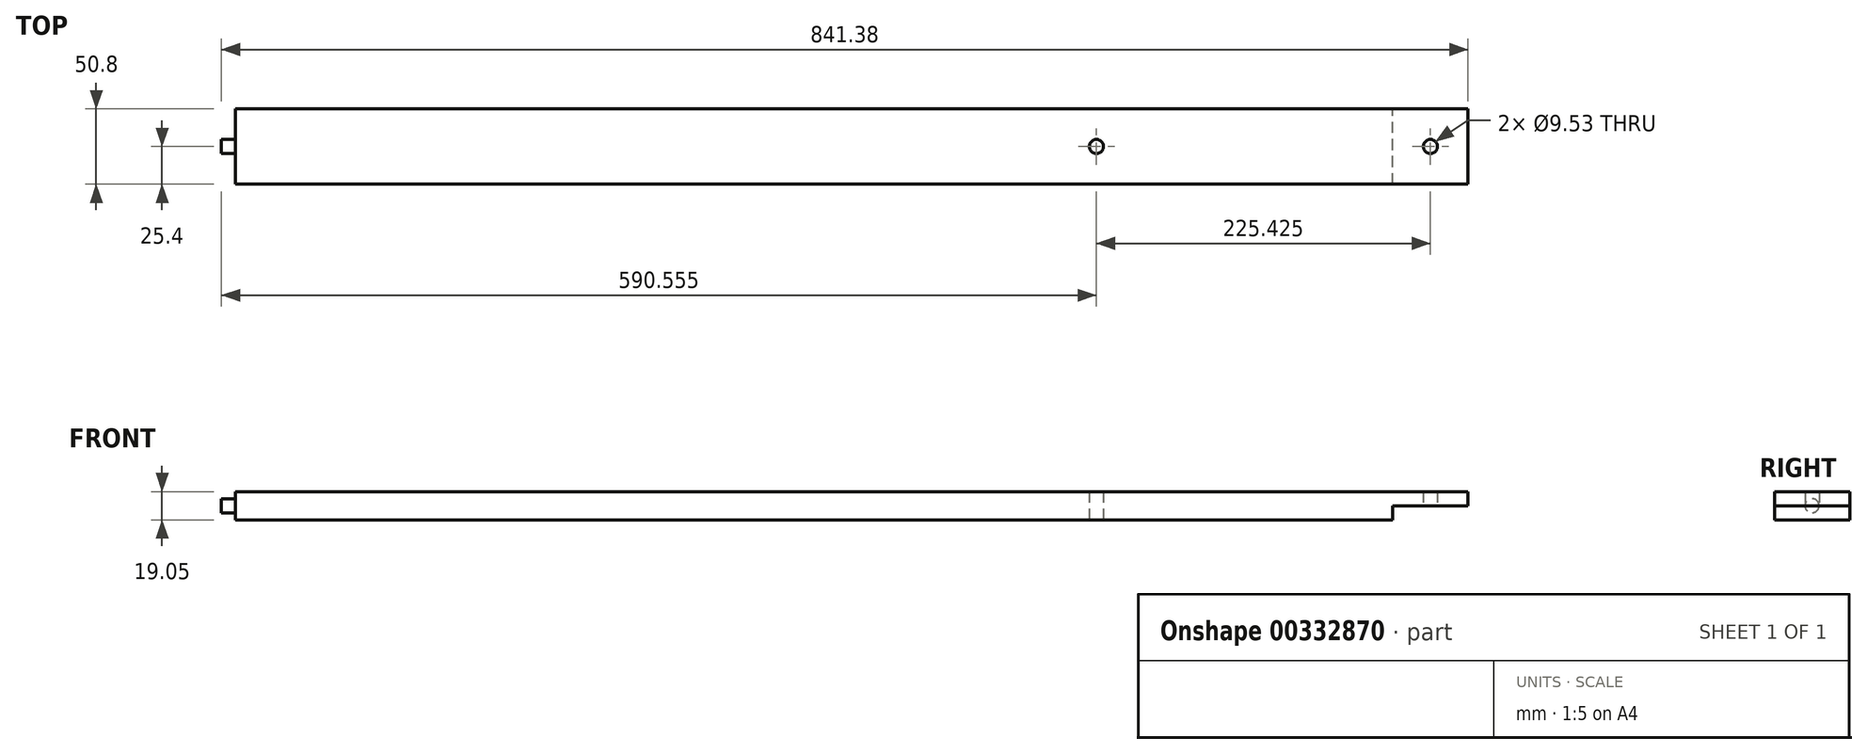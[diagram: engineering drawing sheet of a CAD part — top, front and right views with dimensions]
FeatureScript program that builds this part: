
annotation { "Feature Type Name" : "Feature", "Feature Type Description" : "" }
export const myFeature = defineFeature(function(context is Context, id is Id, definition is map)
    precondition{}
    {
        {
            var Q0;
            Q0=qCreatedBy(makeId("Front.planeOp"),FACE);
            var sketch = newSketch(context, id + "F0", { "sketchPlane" : qUnion([Q0])});
            skLineSegment(sketch, "E0", {"start": v(831.85, 19.05) * mm, "end": v(0, 19.05) * mm});
            skPoint(sketch, "E1.left.start.orphan", {"position": v(-798.41, -3.82) * mm});
            skLineSegment(sketch, "E2.top", {"start": v(781.05, 9.52) * mm, "end": v(831.85, 9.52) * mm});
            skLineSegment(sketch, "E2.left", {"start": v(781.05, 0) * mm, "end": v(781.05, 9.52) * mm});
            skLineSegment(sketch, "E2.right", {"start": v(831.85, 0) * mm, "end": v(831.85, 9.52) * mm});
            skPoint(sketch, "E3.orphan", {"position": v(1631.95, 0) * mm});
            skLineSegment(sketch, "E4", {"start": v(0, 0) * mm, "end": v(0, 19.05) * mm});
            skLineSegment(sketch, "E5", {"start": v(781.05, 0) * mm, "end": v(0, 0) * mm});
            skLineSegment(sketch, "E6", {"start": v(831.85, 9.52) * mm, "end": v(831.85, 19.05) * mm});
            skPoint(sketch, "E7.left.start.orphan", {"position": v(1581.15, 0) * mm});
            skSolve(sketch);
        }
        {
            var Q0;
            Q0=qSketchRegion(id+"F0",true);
            extrude(context, id + "F1", {"entities" : qUnion([Q0]), "depth" : 50.8 * mm});
        }
        {
            var Q0;
            Q0=qCreatedBy(makeId("Top.planeOp"),FACE);
            cPlane(context, id + "F2", {"entities" : qUnion([Q0]), "cplaneType" : CPlaneType.OFFSET, "offset" : 9.52 * mm, "width" : 152.4 * mm, "height" : 152.4 * mm});
        }
        {
            var Q0;
            Q0=qCreatedBy(id+"F2.planeOp",FACE);
            var sketch = newSketch(context, id + "F3", { "sketchPlane" : qUnion([Q0])});
            skCircle(sketch, "E8", {"center": v(806.45, -25.4) * mm, "radius": 4.76 * mm});
            skCircle(sketch, "E9", {"center": v(581.02, -25.4) * mm, "radius": 4.76 * mm});
            skSolve(sketch);
        }
        {
            var Q0;
            Q0=qSketchRegion(id+"F3",true);
            extrude(context, id + "F4", {"entities" : qUnion([Q0]), "operationType" : NewBodyOperationType.REMOVE, "endBound" : BoundingType.SYMMETRIC, "depth" : 25.4 * mm});
        }
        {
            var Q0;
            Q0=qCreatedBy(makeId("Right.planeOp"),FACE);
            var sketch = newSketch(context, id + "F5", { "sketchPlane" : qUnion([Q0])});
            skCircle(sketch, "E10", {"center": v(-25.4, 9.53) * mm, "radius": 4.76 * mm});
            skSolve(sketch);
        }
        {
            var Q0;
            Q0=qSketchRegion(id+"F5",true);
            extrude(context, id + "F6", {"entities" : qUnion([Q0]), "operationType" : NewBodyOperationType.ADD, "oppositeDirection" : true, "depth" : 9.52 * mm});
        }
    });
